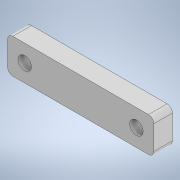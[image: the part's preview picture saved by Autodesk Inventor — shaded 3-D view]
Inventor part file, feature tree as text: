
AUTODESK INVENTOR PART (.ipt)
format: ipt  version: 2020 (Build 240168000, 168)  size: 109,568 bytes
history: native  units: mm
features: extrude x1, fillet x1, sketch x1
ambient origin geometry x8: Origin, YZ Plane, XZ Plane, XY Plane, X Axis, Y Axis, Z Axis, Center Point
bodies: Solid1 (feature_tree)
feature tree (3):
  extrude  "Extrusion1"  Depth=13.0mm
  fillet  "Fillet1"  Radius=5.0mm
  sketch  "Sketch1"  dims[d0=55.0mm d1=13.0mm d2=5.0mm d3=5.0mm d4=42.0mm d5=21.0mm d6=6.5mm d7=6.5mm d8=7.0mm d9=0.0mm d10=2.0mm]
